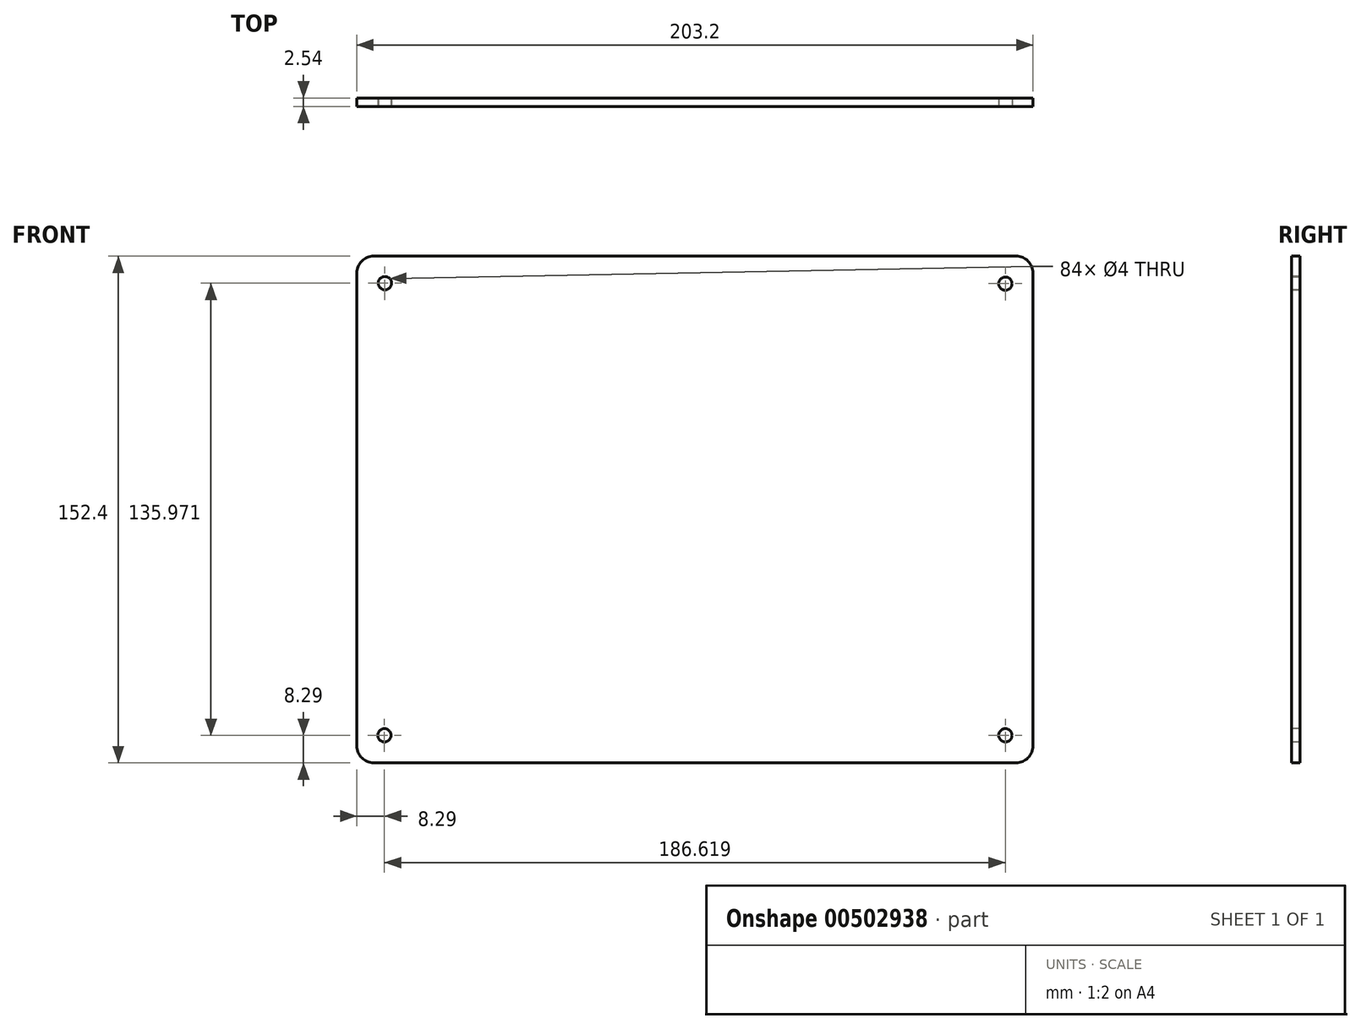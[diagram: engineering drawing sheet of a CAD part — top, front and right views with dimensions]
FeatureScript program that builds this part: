
annotation { "Feature Type Name" : "Feature", "Feature Type Description" : "" }
export const myFeature = defineFeature(function(context is Context, id is Id, definition is map)
    precondition{}
    {
        {
            var Q0;
            Q0=qCreatedBy(makeId("Front.planeOp"),FACE);
            var sketch = newSketch(context, id + "F0", { "sketchPlane" : qUnion([Q0])});
            skLineSegment(sketch, "E0.bottom", {"start": v(0, 0) * mm, "end": v(203.2, 0) * mm});
            skLineSegment(sketch, "E0.top", {"start": v(0, 152.4) * mm, "end": v(203.2, 152.4) * mm});
            skLineSegment(sketch, "E0.left", {"start": v(0, 0) * mm, "end": v(0, 152.4) * mm});
            skLineSegment(sketch, "E0.right", {"start": v(203.2, 0) * mm, "end": v(203.2, 152.4) * mm});
            skSolve(sketch);
        }
        {
            var Q0;
            Q0 = qSketchRegion(id + "F0", true);
            extrude(context, id + "F1", {"entities" : qUnion([Q0]), "depth" : 2.54 * mm});
        }
        {
            var Q0;
            Q0=makeQuery(id+"F1.opExtrude","SWEPT_EDGE",EDGE,{"disambiguationData":[OSD([sQuery(id+"F0.wireOp",EDGE,"E0.top"),sQuery(id+"F0.wireOp",EDGE,"E0.left")])]});
            var Q1;
            Q1=makeQuery(id+"F1.opExtrude","SWEPT_EDGE",EDGE,{"disambiguationData":[OSD([sQuery(id+"F0.wireOp",EDGE,"E0.bottom"),sQuery(id+"F0.wireOp",EDGE,"E0.left")])]});
            var Q2;
            Q2=makeQuery(id+"F1.opExtrude","SWEPT_EDGE",EDGE,{"disambiguationData":[OSD([sQuery(id+"F0.wireOp",EDGE,"E0.bottom"),sQuery(id+"F0.wireOp",EDGE,"E0.right")])]});
            var Q3;
            Q3=makeQuery(id+"F1.opExtrude","SWEPT_EDGE",EDGE,{"disambiguationData":[OSD([sQuery(id+"F0.wireOp",EDGE,"E0.top"),sQuery(id+"F0.wireOp",EDGE,"E0.right")])]});
            fillet(context, id + "F2", {"entities" : qUnion([Q0, Q1, Q2, Q3]), "radius" : 5.08 * mm, "tangentPropagation" : true, "allowEdgeOverflow" : false});
        }
        {
            var Q0;
            Q0=makeQuery(id+"F1.opExtrude","CAP_FACE",FACE,{"disambiguationData":[OSD([sQuery(id+"F0.wireOp",EDGE,"E0.bottom"),sQuery(id+"F0.wireOp",EDGE,"E0.top"),sQuery(id+"F0.wireOp",EDGE,"E0.left"),sQuery(id+"F0.wireOp",EDGE,"E0.right")])],"isStart":false});
            var sketch = newSketch(context, id + "F3", { "sketchPlane" : qUnion([Q0])});
            skCircle(sketch, "E1", {"center": v(8.44, 144.26) * mm, "radius": 2 * mm});
            skCircle(sketch, "E2", {"center": v(8.3, 8.3) * mm, "radius": 2 * mm});
            skCircle(sketch, "E3", {"center": v(194.9, 144.1) * mm, "radius": 2 * mm});
            skCircle(sketch, "E4", {"center": v(194.9, 8.3) * mm, "radius": 2 * mm});
            skSolve(sketch);
        }
        {
            var Q0;
            Q0=sQuery(id+"F3.wireOp",VERTEX,"E1.center");
            var Q1;
            Q1=sQuery(id+"F3.wireOp",VERTEX,"E3.center");
            var Q2;
            Q2=sQuery(id+"F3.wireOp",VERTEX,"E4.center");
            var Q3;
            Q3=sQuery(id+"F3.wireOp",VERTEX,"E2.center");
            var Q4;
            Q4=makeQuery(id+"F1.opExtrude","SWEPT_BODY",BODY,{"disambiguationData":[OSD([sQuery(id+"F0.wireOp",EDGE,"E0.bottom"),sQuery(id+"F0.wireOp",EDGE,"E0.top"),sQuery(id+"F0.wireOp",EDGE,"E0.left"),sQuery(id+"F0.wireOp",EDGE,"E0.right")])]});
            hole(context, id + "F4", {"style" : HoleStyle.SIMPLE, "endStyle" : HoleEndStyle.THROUGH, "holeDiameter" : 4 * mm, "isTappedThrough" : true, "tappedDepth" : 12.7 * mm, "tapClearance" : 3, "startFromSketch" : true, "locations" : qUnion([Q0, Q1, Q2, Q3]), "scope" : qUnion([Q4])});
        }
    });
